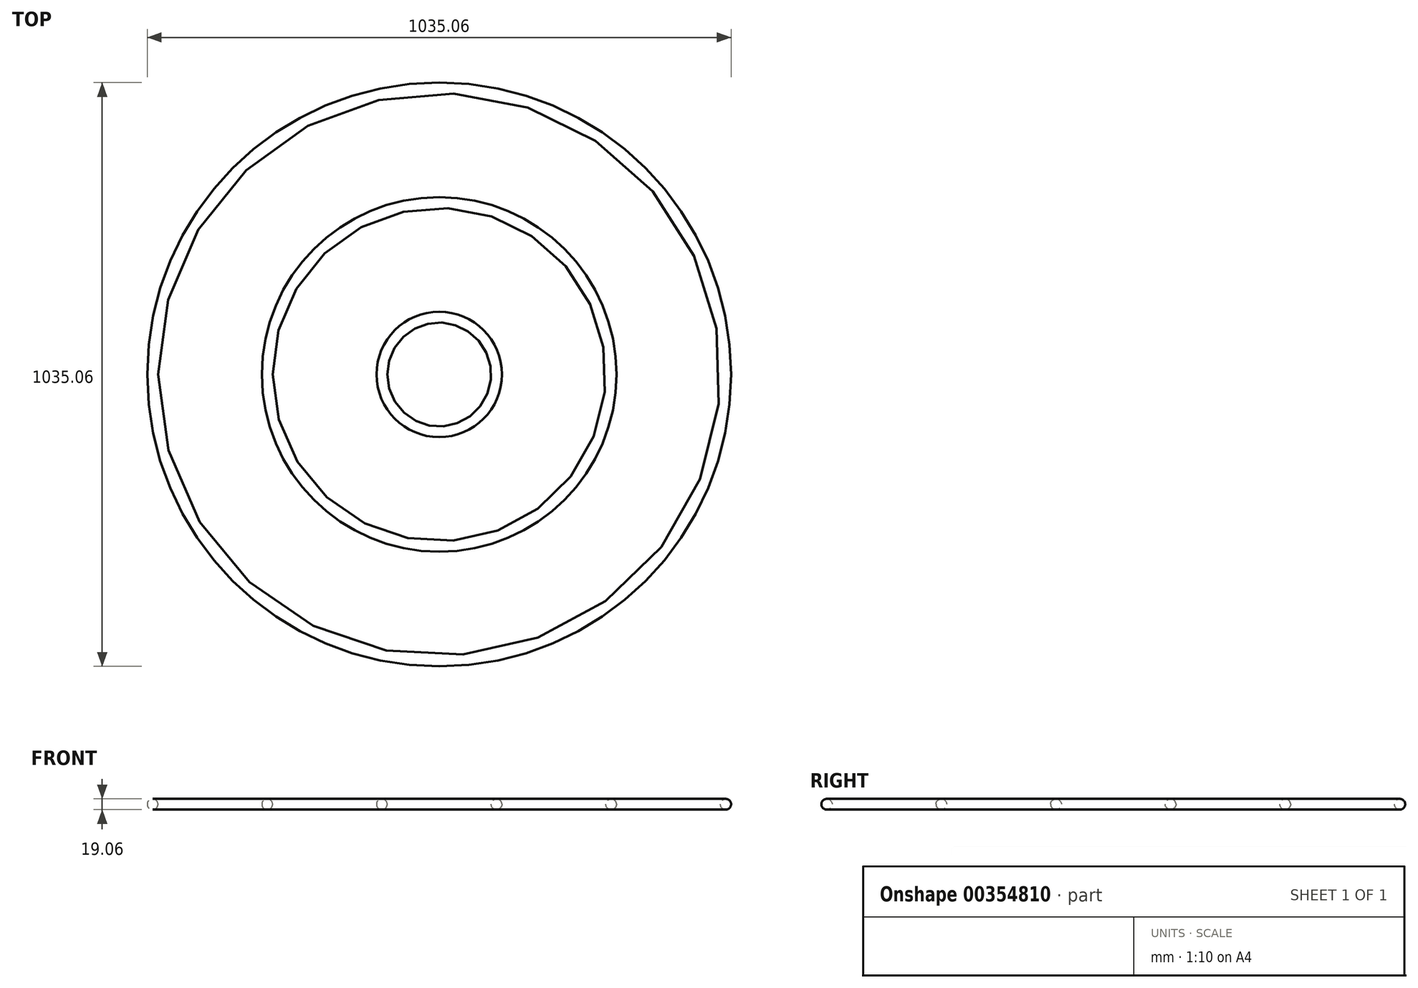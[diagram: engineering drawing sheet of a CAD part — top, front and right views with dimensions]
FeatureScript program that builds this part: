
annotation { "Feature Type Name" : "Feature", "Feature Type Description" : "" }
export const myFeature = defineFeature(function(context is Context, id is Id, definition is map)
    precondition{}
    {
        {
            var Q0;
            Q0=qCreatedBy(makeId("Front.planeOp"),FACE);
            var sketch = newSketch(context, id + "F0", { "sketchPlane" : qUnion([Q0])});
            skCircle(sketch, "E0", {"center": v(101.6, 0) * mm, "radius": 9.53 * mm});
            skCircle(sketch, "E1", {"center": v(304.8, 0) * mm, "radius": 9.53 * mm});
            skCircle(sketch, "E2", {"center": v(508, 0) * mm, "radius": 9.53 * mm});
            skLineSegment(sketch, "E3", {"start": v(0, 0) * mm, "end": v(0, 66.94) * mm});
            skSolve(sketch);
        }
        {
            var Q0;
            Q0 = qSketchRegion(id + "F0", true);
            var Q1;
            Q1=sQuery(id+"F0.wireOp",EDGE,"E3");
            revolve(context, id + "F1", {"entities" : qUnion([Q0]), "axis" : qUnion([Q1]), "revolveType" : RevolveType.FULL});
        }
    });
